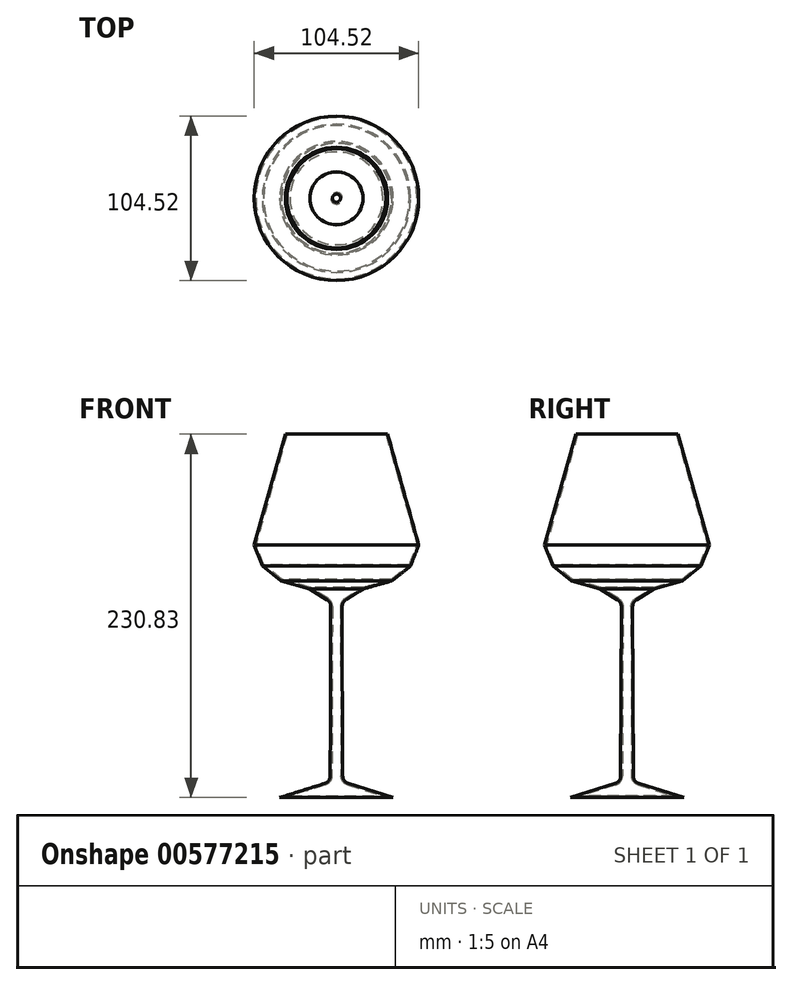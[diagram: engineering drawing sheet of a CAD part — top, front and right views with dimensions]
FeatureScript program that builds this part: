
annotation { "Feature Type Name" : "Feature", "Feature Type Description" : "" }
export const myFeature = defineFeature(function(context is Context, id is Id, definition is map)
    precondition{}
    {
        {
            var Q0;
            Q0=qCreatedBy(makeId("Front.planeOp"),FACE);
            var sketch = newSketch(context, id + "F0", { "sketchPlane" : qUnion([Q0])});
            skLineSegment(sketch, "E0", {"start": v(-32.5, 234.38) * mm, "end": v(0, 234.38) * mm});
            skLineSegment(sketch, "E1", {"start": v(-32.5, 234.38) * mm, "end": v(-52.26, 163.97) * mm});
            skLineSegment(sketch, "E2", {"start": v(-52.26, 163.97) * mm, "end": v(-47.09, 150.56) * mm});
            skLineSegment(sketch, "E3", {"start": v(-47.09, 150.56) * mm, "end": v(-35.28, 141.16) * mm});
            skLineSegment(sketch, "E4", {"start": v(-35.28, 141.16) * mm, "end": v(-17.22, 136.1) * mm});
            skLineSegment(sketch, "E5", {"start": v(-3.6, 127.55) * mm, "end": v(-4, 13.57) * mm});
            skLineSegment(sketch, "E6", {"start": v(-4, 13.57) * mm, "end": v(-36.05, 3.55) * mm});
            skLineSegment(sketch, "E7", {"start": v(-36.05, 3.55) * mm, "end": v(0, 3.55) * mm});
            skLineSegment(sketch, "E8", {"start": v(0, 234.38) * mm, "end": v(0, 3.55) * mm});
            skLineSegment(sketch, "E9", {"start": v(-17.22, 136.1) * mm, "end": v(-3.6, 127.55) * mm});
            skLineSegment(sketch, "E10", {"start": v(0, 3.55) * mm, "end": v(0, 13.55) * mm, "construction": true});
            skSolve(sketch);
        }
        {
            var Q0;
            Q0 = qSketchRegion(id + "F0", true);
            var Q1;
            Q1=sQuery(id+"F0.wireOp",EDGE,"E8");
            revolve(context, id + "F1", {"entities" : qUnion([Q0]), "axis" : qUnion([Q1]), "revolveType" : RevolveType.FULL});
        }
        {
            var Q0;
            Q0=makeQuery(id+"F1.opRevolve","SWEPT_EDGE",EDGE,{"disambiguationData":[OSD([sQuery(id+"F0.wireOp",EDGE,"E5"),sQuery(id+"F0.wireOp",EDGE,"E6")])]});
            var Q1;
            Q1=makeQuery(id+"F1.opRevolve","SWEPT_EDGE",EDGE,{"disambiguationData":[OSD([sQuery(id+"F0.wireOp",EDGE,"E5"),sQuery(id+"F0.wireOp",EDGE,"E9")])]});
            fillet(context, id + "F2", {"entities" : qUnion([Q0, Q1]), "radius" : 5 * mm, "tangentPropagation" : true, "allowEdgeOverflow" : false});
        }
        {
            var Q0;
            Q0=makeQuery(id+"F1.opRevolve","SWEPT_FACE",FACE,{"disambiguationData":[OSD([sQuery(id+"F0.wireOp",EDGE,"E0")])]});
            shell(context, id + "F3", {"entities" : qUnion([Q0]), "thickness" : 1 * mm});
        }
    });
